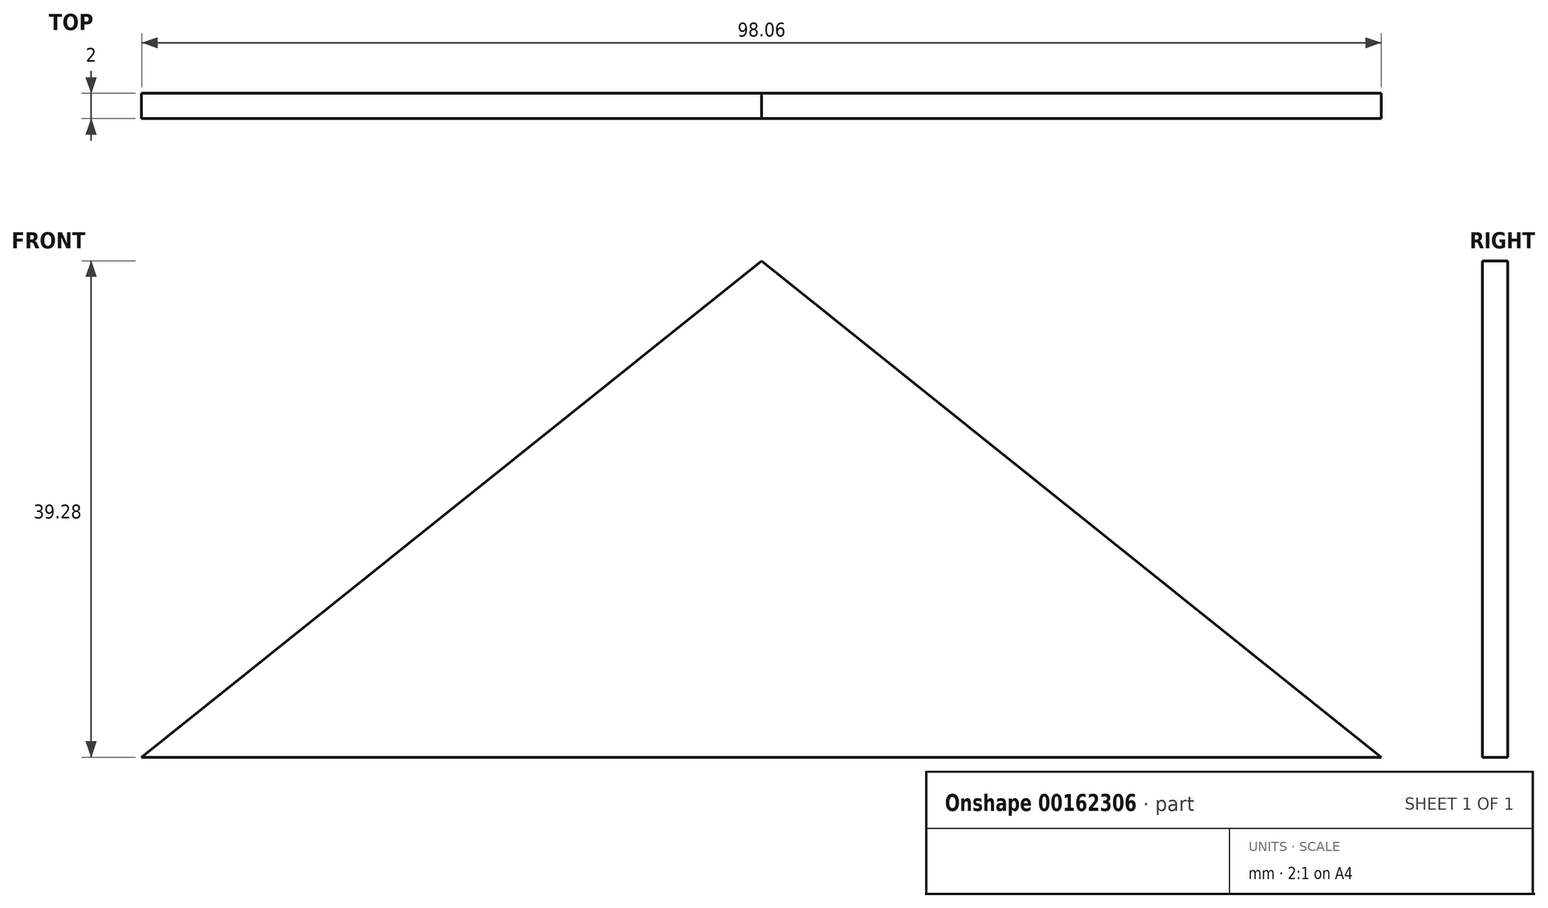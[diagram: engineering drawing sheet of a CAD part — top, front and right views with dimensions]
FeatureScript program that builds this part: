
annotation { "Feature Type Name" : "Feature", "Feature Type Description" : "" }
export const myFeature = defineFeature(function(context is Context, id is Id, definition is map)
    precondition{}
    {
        {
            var Q0;
            Q0=qCreatedBy(makeId("Front.planeOp"),FACE);
            var sketch = newSketch(context, id + "F0", { "sketchPlane" : qUnion([Q0])});
            skLineSegment(sketch, "E0", {"start": v(0, 39.28) * mm, "end": v(49.03, 0) * mm});
            skLineSegment(sketch, "E1.MirrorCS", {"start": v(0, 39.28) * mm, "end": v(-49.03, 0) * mm});
            skLineSegment(sketch, "E2", {"start": v(-49.03, 0) * mm, "end": v(49.03, 0) * mm});
            skSolve(sketch);
        }
        {
            var Q0;
            Q0=qSketchRegion(id+"F0",true);
            extrude(context, id + "F1", {"entities" : qUnion([Q0]), "depth" : 2 * mm});
        }
    });
